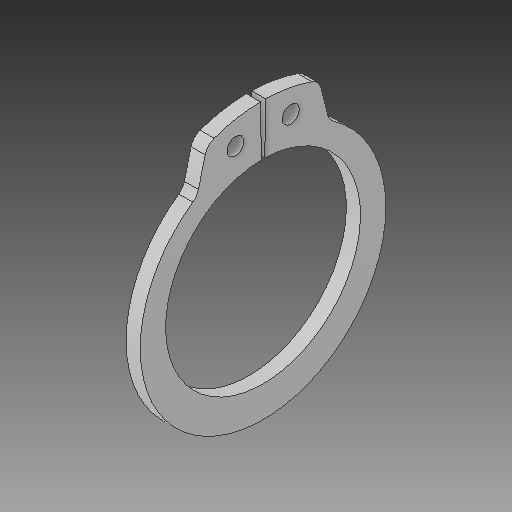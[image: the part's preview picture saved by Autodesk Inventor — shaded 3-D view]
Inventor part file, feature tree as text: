
AUTODESK INVENTOR PART (.ipt)
format: ipt  version: 2018 (Build 220112000, 112)  size: 111,104 bytes
history: native  units: in
note: dims shown in document units (in); Inventor stores cm internally (conversion verified against a paired STEP export)
features: fillet x1
ambient origin geometry x8: Origin, YZ Plane, XZ Plane, XY Plane, X Axis, Y Axis, Z Axis, Center Point
bodies: Solid1 (feature_tree)
feature tree (1):
  fillet  "Fillet1"  [1 undecoded]
note: 1 required parameter value undecoded (feature->parameter linkage not recoverable at this tier; creation-order binding heuristic only, values carry confidence <= 0.55)
